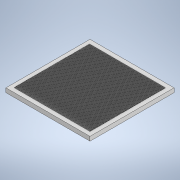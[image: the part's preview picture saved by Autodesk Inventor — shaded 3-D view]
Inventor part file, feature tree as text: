
AUTODESK INVENTOR PART (.ipt)
format: ipt  version: 2021 (Build 250183000, 183)  size: 329,728 bytes
history: native  units: mm
features: extrude x2, sketch x2, pattern_linear x1
ambient origin geometry x8: Origin, YZ Plane, XZ Plane, XY Plane, X Axis, Y Axis, Z Axis, Center Point
bodies: Solid1 (feature_tree)
feature tree (5):
  extrude  "Extrusion1"  Depth=200.0mm
  extrude  "Extrusion2"  Depth=180.0mm
  pattern_linear  "Rectangular Pattern1"  Spacing1=1.0mm  [1 undecoded]
  sketch  "Sketch1"  dims[d0=200.0mm d1=200.0mm]
  sketch  "Sketch2"  dims[d2=10.0mm d3=0.0mm d4=180.0mm d5=1.0mm d6=1.0mm d7=0.0mm d8=900.0mm d10=2.0mm]
note: 1 required parameter value undecoded (feature->parameter linkage not recoverable at this tier; creation-order binding heuristic only, values carry confidence <= 0.55)
